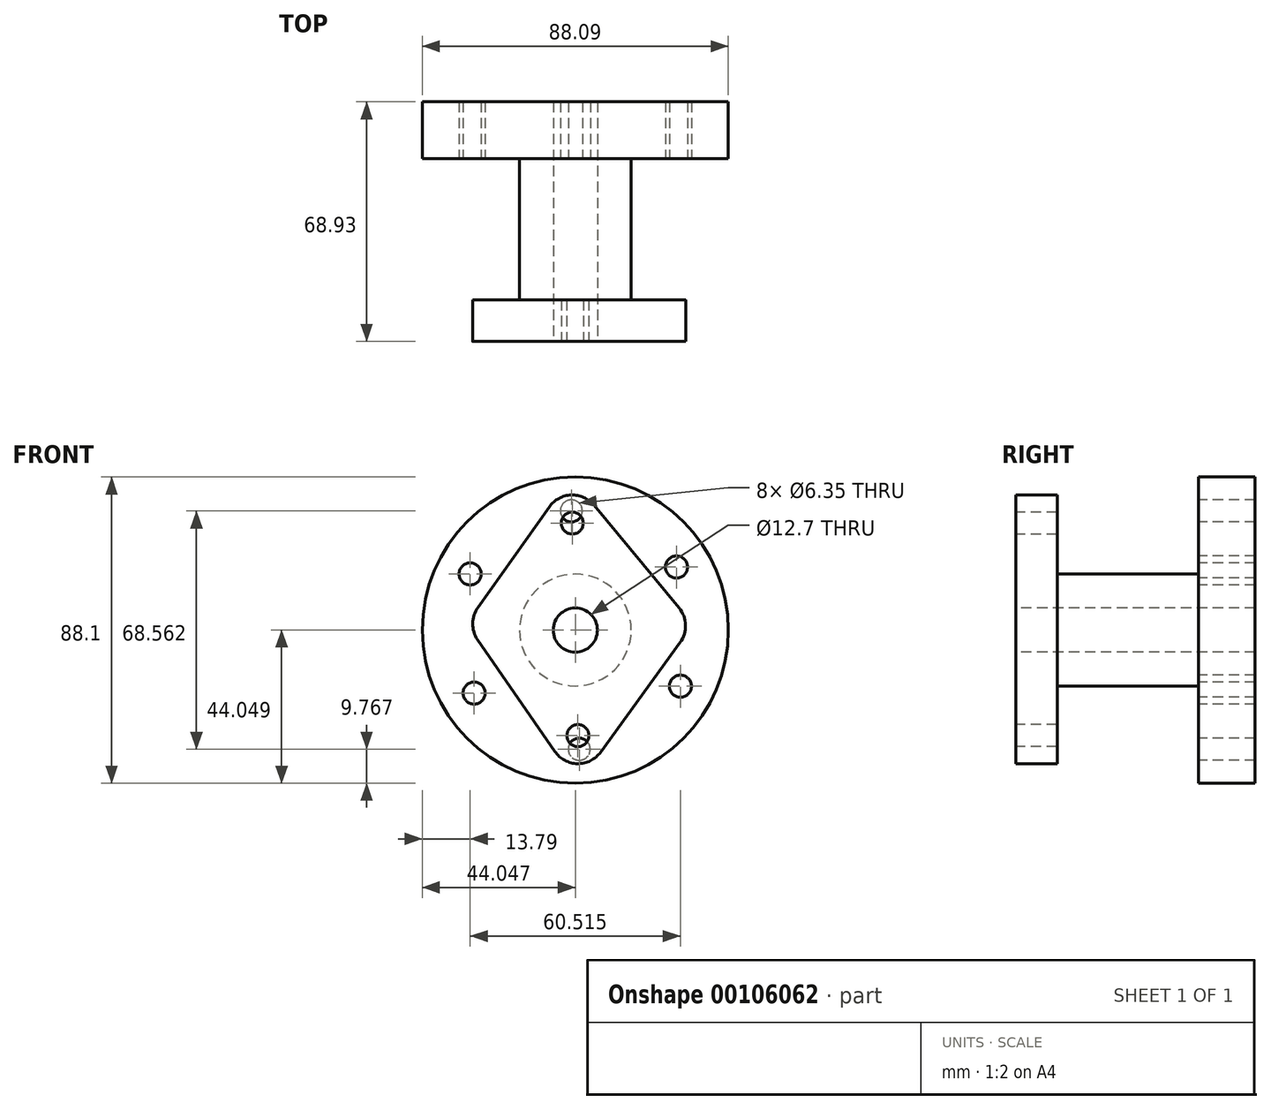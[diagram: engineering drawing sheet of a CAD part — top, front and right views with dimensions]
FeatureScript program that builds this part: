
annotation { "Feature Type Name" : "Feature", "Feature Type Description" : "" }
export const myFeature = defineFeature(function(context is Context, id is Id, definition is map)
    precondition{}
    {
        {
            var Q0;
            Q0=qCreatedBy(makeId("Front.planeOp"),FACE);
            var sketch = newSketch(context, id + "F0", { "sketchPlane" : qUnion([Q0])});
            skCircle(sketch, "E0", {"center": v(-3.33, -6.7) * mm, "radius": 44.05 * mm});
            skSolve(sketch);
        }
        {
            var Q0;
            Q0=makeQuery(id+"F0.imprint","IMPRINT",FACE,{"disambiguationData":[TD([[makeQuery(id+"F0.imprint","IMPRINT",EDGE,{"derivedFrom":sQuery(id+"F0.wireOp",EDGE,"E0")}),1.0]])]});
            extrude(context, id + "F1", {"entities" : qUnion([Q0]), "depth" : 16.36 * mm});
        }
        {
            var Q0;
            Q0=makeQuery(id+"F1.opExtrude","CAP_FACE",FACE,{"disambiguationData":[OSD([sQuery(id+"F0.wireOp",EDGE,"E0")])],"isStart":false});
            var sketch = newSketch(context, id + "F2", { "sketchPlane" : qUnion([Q0])});
            skCircle(sketch, "E1", {"center": v(-4.47, 27.58) * mm, "radius": 2.96 * mm});
            skCircle(sketch, "E2.1.0", {"center": v(-33.59, 9.45) * mm, "radius": 2.96 * mm});
            skCircle(sketch, "E2.2.0", {"center": v(-32.45, -24.83) * mm, "radius": 2.96 * mm});
            skCircle(sketch, "E2.3.0", {"center": v(-2.2, -40.98) * mm, "radius": 2.96 * mm});
            skCircle(sketch, "E2.4.0", {"center": v(26.92, -22.86) * mm, "radius": 2.96 * mm});
            skCircle(sketch, "E2.5.0", {"center": v(25.79, 11.42) * mm, "radius": 2.96 * mm});
            skPoint(sketch, "E2.center", {"position": v(-3.33, -6.7) * mm});
            skSolve(sketch);
        }
        {
            var Q0;
            Q0=sQuery(id+"F2.wireOp",VERTEX,"E1.center");
            var Q1;
            Q1=sQuery(id+"F2.wireOp",VERTEX,"E2.5.0.center");
            var Q2;
            Q2=sQuery(id+"F2.wireOp",VERTEX,"E2.4.0.center");
            var Q3;
            Q3=sQuery(id+"F2.wireOp",VERTEX,"E2.3.0.center");
            var Q4;
            Q4=sQuery(id+"F2.wireOp",VERTEX,"E2.1.0.center");
            var Q5;
            Q5=sQuery(id+"F2.wireOp",VERTEX,"E2.2.0.center");
            var Q6;
            Q6=makeQuery(id+"F1.opExtrude","SWEPT_BODY",BODY,{"disambiguationData":[OSD([sQuery(id+"F0.wireOp",EDGE,"E0")])]});
            hole(context, id + "F3", {"style" : HoleStyle.SIMPLE, "endStyle" : HoleEndStyle.THROUGH, "holeDiameter" : 6.35 * mm, "locations" : qUnion([Q0, Q1, Q2, Q3, Q4, Q5]), "scope" : qUnion([Q6]), "isTappedThrough" : true});
        }
        {
            var Q0;
            Q0=makeQuery(id+"F1.opExtrude","CAP_FACE",FACE,{"disambiguationData":[OSD([sQuery(id+"F0.wireOp",EDGE,"E0")])],"isStart":false});
            var sketch = newSketch(context, id + "F4", { "sketchPlane" : qUnion([Q0])});
            skCircle(sketch, "E3", {"center": v(-3.33, -6.7) * mm, "radius": 16.08 * mm});
            skSolve(sketch);
        }
        {
            var Q0;
            Q0=makeQuery(id+"F4.imprint","IMPRINT",FACE,{"disambiguationData":[TD([[makeQuery(id+"F4.imprint","IMPRINT",EDGE,{"derivedFrom":sQuery(id+"F4.wireOp",EDGE,"E3")}),1.0]])]});
            extrude(context, id + "F5", {"entities" : qUnion([Q0]), "operationType" : NewBodyOperationType.ADD, "depth" : 40.63 * mm});
        }
        {
            var Q0;
            Q0=makeQuery(id+"F5.opExtrude","CAP_FACE",FACE,{"disambiguationData":[OSD([sQuery(id+"F4.wireOp",EDGE,"E3")])],"isStart":false});
            var sketch = newSketch(context, id + "F6", { "sketchPlane" : qUnion([Q0])});
            skCircle(sketch, "E4", {"center": v(-3.33, -6.7) * mm, "radius": 6.26 * mm});
            skSolve(sketch);
        }
        {
            var Q0;
            Q0=sQuery(id+"F6.wireOp",VERTEX,"E4.center");
            var Q1;
            Q1=makeQuery(id+"F1.opExtrude","SWEPT_BODY",BODY,{"disambiguationData":[OSD([sQuery(id+"F0.wireOp",EDGE,"E0")])]});
            hole(context, id + "F7", {"style" : HoleStyle.SIMPLE, "endStyle" : HoleEndStyle.THROUGH, "holeDiameter" : 12.7 * mm, "locations" : qUnion([Q0]), "scope" : qUnion([Q1]), "isTappedThrough" : true});
        }
        {
            var Q0;
            Q0=makeQuery(id+"F5.opExtrude","CAP_FACE",FACE,{"disambiguationData":[OSD([sQuery(id+"F4.wireOp",EDGE,"E3")])],"isStart":false});
            var sketch = newSketch(context, id + "F8", { "sketchPlane" : qUnion([Q0])});
            skLineSegment(sketch, "E5", {"start": v(-4.7, 37.31) * mm, "end": v(-34.67, -4.8) * mm});
            skLineSegment(sketch, "E6", {"start": v(-34.67, -4.8) * mm, "end": v(-2.74, -51.02) * mm});
            skLineSegment(sketch, "E7", {"start": v(-2.74, -51.02) * mm, "end": v(30.55, -5.2) * mm});
            skLineSegment(sketch, "E8", {"start": v(30.55, -5.2) * mm, "end": v(-4.7, 37.31) * mm});
            skSolve(sketch);
        }
        {
            var Q0;
            Q0=makeQuery(id+"F8.imprint","IMPRINT",FACE,{"disambiguationData":[TD([[makeQuery(id+"F8.imprint","IMPRINT",EDGE,{"derivedFrom":makeQuery(id+"F5.opExtrude","CAP_EDGE",EDGE,{"disambiguationData":[OSD([sQuery(id+"F4.wireOp",EDGE,"E3")])],"isStart":false})}),1.0]])]});
            var Q1;
            Q1=makeQuery(id+"F8.imprint","IMPRINT",FACE,{"disambiguationData":[TD([[makeQuery(id+"F8.imprint","IMPRINT",EDGE,{"derivedFrom":sQuery(id+"F8.wireOp",EDGE,"E5")}),1.0]])]});
            extrude(context, id + "F9", {"entities" : qUnion([Q0, Q1]), "operationType" : NewBodyOperationType.ADD, "depth" : 17.92 * mm});
        }
        {
            var Q0;
            Q0=makeQuery(id+"F9.opExtrude","SWEPT_EDGE",EDGE,{"disambiguationData":[OSD([sQuery(id+"F8.wireOp",EDGE,"E5"),sQuery(id+"F8.wireOp",EDGE,"E8")])]});
            var Q1;
            Q1=makeQuery(id+"F9.opExtrude","SWEPT_EDGE",EDGE,{"disambiguationData":[OSD([sQuery(id+"F8.wireOp",EDGE,"E5"),sQuery(id+"F8.wireOp",EDGE,"E6")])]});
            var Q2;
            Q2=makeQuery(id+"F9.opExtrude","SWEPT_EDGE",EDGE,{"disambiguationData":[OSD([sQuery(id+"F8.wireOp",EDGE,"E7"),sQuery(id+"F8.wireOp",EDGE,"E8")])]});
            var Q3;
            Q3=makeQuery(id+"F9.opExtrude","SWEPT_EDGE",EDGE,{"disambiguationData":[OSD([sQuery(id+"F8.wireOp",EDGE,"E6"),sQuery(id+"F8.wireOp",EDGE,"E7")])]});
            fillet(context, id + "F10", {"entities" : qUnion([Q0, Q1, Q2, Q3]), "radius" : 8.06 * mm, "tangentPropagation" : true, "allowEdgeOverflow" : false});
        }
        {
            var Q0;
            Q0=makeQuery(id+"F9.opExtrude","CAP_FACE",FACE,{"disambiguationData":[OSD([sQuery(id+"F7.hole-0.sketch.wireOp",EDGE,"core_line_2"),sQuery(id+"F7.hole-0.sketch.wireOp",EDGE,"core_line_3"),sQuery(id+"F8.wireOp",EDGE,"E5"),sQuery(id+"F8.wireOp",EDGE,"E6"),sQuery(id+"F8.wireOp",EDGE,"E7"),sQuery(id+"F8.wireOp",EDGE,"E8")])],"isStart":false});
            var sketch = newSketch(context, id + "F11", { "sketchPlane" : qUnion([Q0])});
            skCircle(sketch, "E9", {"center": v(-4.21, 24.1) * mm, "radius": 3.54 * mm});
            skCircle(sketch, "E10", {"center": v(-2.58, -37.07) * mm, "radius": 3.54 * mm});
            skSolve(sketch);
        }
        {
            var Q0;
            Q0=sQuery(id+"F11.wireOp",VERTEX,"E9.center");
            var Q1;
            Q1=sQuery(id+"F11.wireOp",VERTEX,"E10.center");
            var Q2;
            Q2=makeQuery(id+"F1.opExtrude","SWEPT_BODY",BODY,{"disambiguationData":[OSD([sQuery(id+"F0.wireOp",EDGE,"E0")])]});
            hole(context, id + "F12", {"style" : HoleStyle.SIMPLE, "endStyle" : HoleEndStyle.BLIND, "holeDiameter" : 6.35 * mm, "holeDepth" : 50.8 * mm, "locations" : qUnion([Q0, Q1]), "scope" : qUnion([Q2])});
        }
        {
            var Q0;
            Q0=makeQuery(id+"F9.opExtrude","CAP_FACE",FACE,{"disambiguationData":[OSD([sQuery(id+"F7.hole-0.sketch.wireOp",EDGE,"core_line_2"),sQuery(id+"F7.hole-0.sketch.wireOp",EDGE,"core_line_3"),sQuery(id+"F8.wireOp",EDGE,"E5"),sQuery(id+"F8.wireOp",EDGE,"E6"),sQuery(id+"F8.wireOp",EDGE,"E7"),sQuery(id+"F8.wireOp",EDGE,"E8")])],"isStart":false});
            extrude(context, id + "F13", {"entities" : qUnion([Q0]), "operationType" : NewBodyOperationType.REMOVE, "oppositeDirection" : true, "depth" : 6 * mm});
        }
    });
